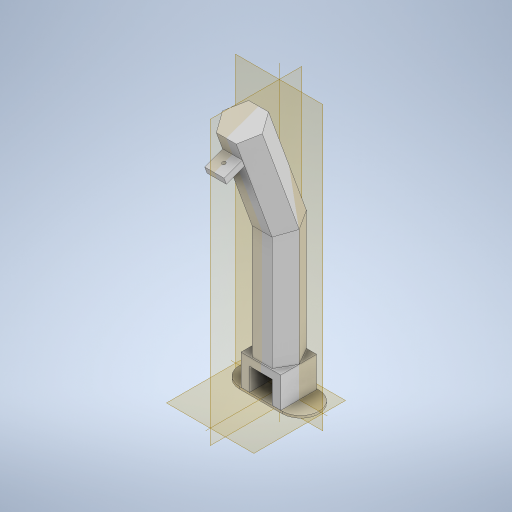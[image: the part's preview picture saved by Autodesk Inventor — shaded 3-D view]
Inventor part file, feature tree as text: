
AUTODESK INVENTOR PART (.ipt)
format: ipt  version: 2023 (Build 270158000, 158)  size: 326,656 bytes
history: native  units: in
note: dims shown in document units (in); Inventor stores cm internally (conversion verified against a paired STEP export)
features: sketch x7, extrude x4, sweep x1, hole x1
ambient origin geometry x8: Origin, YZ Plane, XZ Plane, XY Plane, X Axis, Y Axis, Z Axis, Center Point
bodies: Solid1 (feature_tree)
feature tree (13):
  sweep  "Sweep1"
  extrude  "Extrusion1"  Depth=1.0994in
  hole  "Hole1"  [1 undecoded]
  extrude  "Extrusion2"  Depth=0.2362in
  extrude  "Extrusion3"  Depth=0.6693in TaperAngle=0.0deg
  extrude  "Extrusion4"  Depth=0.1969in
  sketch  "Sketch1"  dims[d1=0.689in d5=5.1181in]
  sketch  "Sketch3"  dims[d6=3.7402in d7=1.0994in]
  sketch  "Sketch4"  dims[d8=0.0in d9=0.0in d10=0.6299in]
  sketch  "Sketch5"  dims[d11=0.3346in d12=0.2362in]
  sketch  "Sketch6"  dims[d13=0.6693in d14=0.6693in d15=0.0in]
  sketch  "Sketch7"  dims[d16=0.315in d17=0.1969in]
  sketch  "Sketch8"  dims[d18=0.1181in d19=0.2362in d20=0.1575in d21=0.0787in d22=90.0deg d23=0.3967in d24=0.8108in d25=1.063in d26=0.0in d27=0.3937in d28=0.7874in d29=0.7874in d30=1.9685in d31=0.0in d32=1.378in d33=2.7559in d34=0.0787in d35=0.0in]
note: 1 required parameter value undecoded (feature->parameter linkage not recoverable at this tier; creation-order binding heuristic only, values carry confidence <= 0.55)
